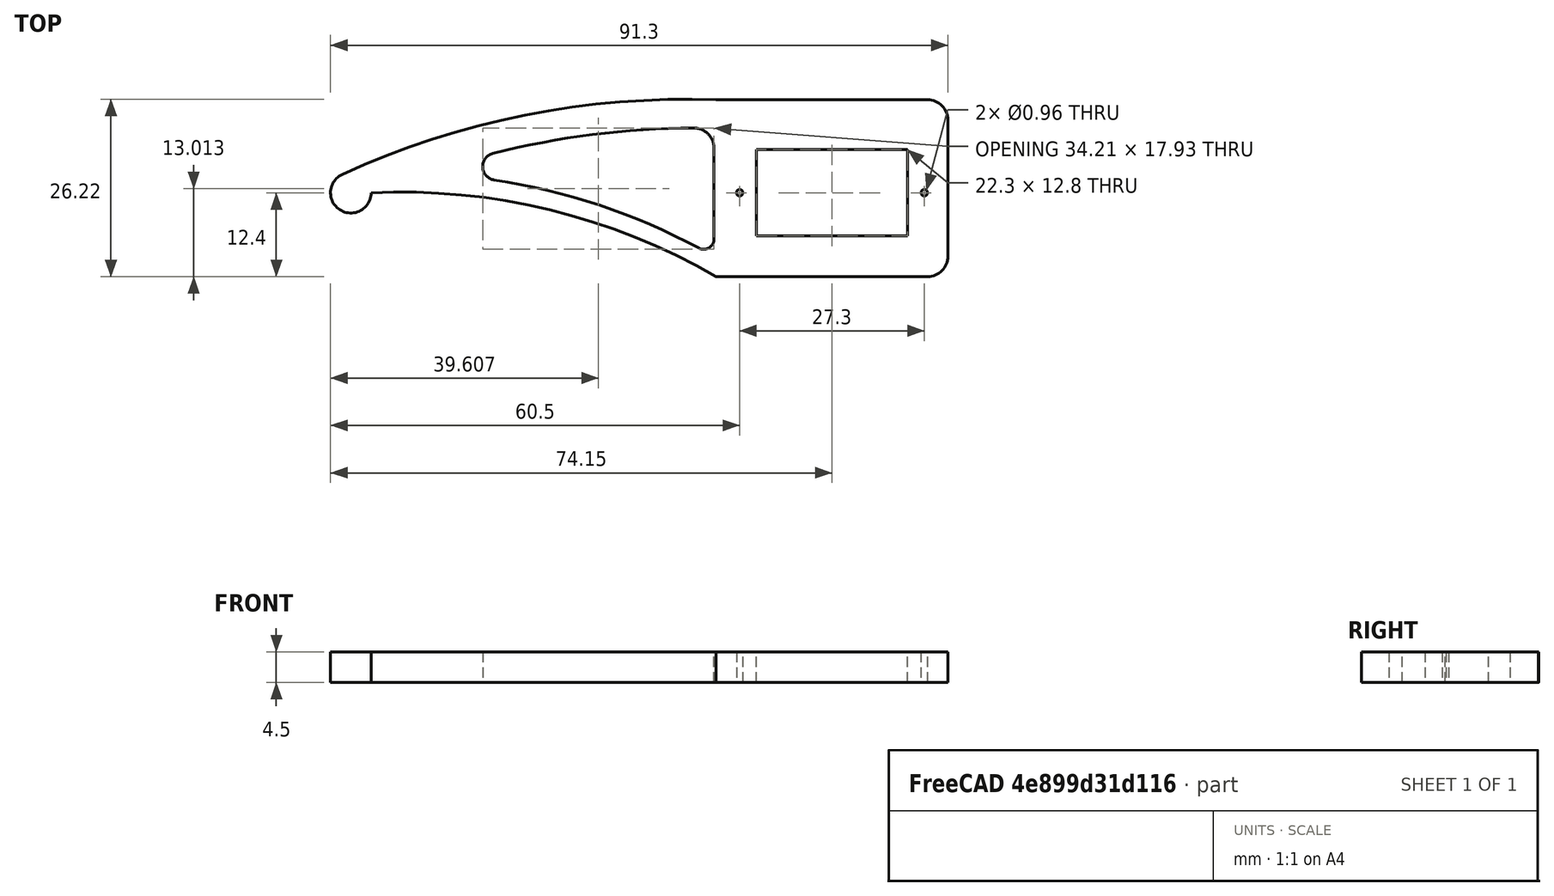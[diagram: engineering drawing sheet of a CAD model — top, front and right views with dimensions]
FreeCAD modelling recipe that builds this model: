
FCSTD DOCUMENT  (FreeCAD 0.21R33771 (Git))
Label: temp_work
License: All rights reserved
LicenseURL: https://en.wikipedia.org/wiki/All_rights_reserved
objects: Sketcher::SketchObject×1, PartDesign::Pad×1, PartDesign::Body×1
note: 4 computed .brp shape members not serialized (recipe doc carries the construction recipe); baked Part::Feature solids carry a one-line shape summary decoded from their .brp

FEATURE [Sketcher::SketchObject] Sketch
  FullyConstrained = true
  MapMode = 5
  Support = -> [XY_Plane]
  sketch-geometry (24):
    g0: LineSegment StartX=-11.15 StartY=-6.4 StartZ=0 EndX=-11.15 EndY=6.4 EndZ=0
    g1: LineSegment StartX=-11.15 StartY=6.4 StartZ=0 EndX=11.15 EndY=6.4 EndZ=0
    g2: LineSegment StartX=11.15 StartY=6.4 StartZ=0 EndX=11.15 EndY=-6.4 EndZ=0
    g3: LineSegment StartX=11.15 StartY=-6.4 StartZ=0 EndX=-11.15 EndY=-6.4 EndZ=0
    g4: GeomPoint X=0 Y=0 Z=0
    g5: LineSegment StartX=-17.44 StartY=6.58002 StartZ=0 EndX=-17.44 EndY=-6.81401 EndZ=0
    g6: LineSegment StartX=-17.15 StartY=-12.4 StartZ=0 EndX=14.15 EndY=-12.4 EndZ=0
    g7: LineSegment StartX=17.15 StartY=-9.4 StartZ=0 EndX=17.15 EndY=10.742 EndZ=0
    g8: LineSegment StartX=14.15 StartY=13.742 StartZ=0 EndX=-17.15 EndY=13.742 EndZ=0
    g9: GeomPoint X=0 Y=0 Z=0
    g10: ArcOfCircle CenterX=14.15 CenterY=10.742 CenterZ=0 NormalX=0 NormalY=0 NormalZ=1 AngleXU=0 Radius=3 StartAngle=0 EndAngle=1.5708
    g11: GeomPoint X=17.15 Y=13.742 Z=0
    g12: ArcOfCircle CenterX=14.15 CenterY=-9.4 CenterZ=0 NormalX=0 NormalY=0 NormalZ=1 AngleXU=0 Radius=3 StartAngle=4.71239 EndAngle=6.28319
    g13: GeomPoint X=17.15 Y=-12.4 Z=0
    g14: Circle CenterX=-13.65 CenterY=0 CenterZ=0 NormalX=0 NormalY=0 NormalZ=1 AngleXU=0 Radius=0.48
    g15: Circle CenterX=13.65 CenterY=0 CenterZ=0 NormalX=0 NormalY=0 NormalZ=1 AngleXU=0 Radius=0.48
    g16: ArcOfCircle CenterX=-71.15 CenterY=0 CenterZ=0 NormalX=0 NormalY=0 NormalZ=1 AngleXU=0 Radius=3 StartAngle=2.00057 EndAngle=6.28318
    g17: ArcOfCircle CenterX=-21.5667 CenterY=-108.178 CenterZ=0 NormalX=0 NormalY=0 NormalZ=1 AngleXU=0 Radius=122 StartAngle=1.53459 EndAngle=2.00057
    g18: ArcOfCircle CenterX=-20.0433 CenterY=-112.419 CenterZ=0 NormalX=0 NormalY=0 NormalZ=1 AngleXU=0 Radius=122 StartAngle=1.57413 EndAngle=1.82008
    g19: ArcOfCircle CenterX=-63.6795 CenterY=-92.6923 CenterZ=0 NormalX=0 NormalY=0 NormalZ=1 AngleXU=0 Radius=92.8 StartAngle=1.04559 EndAngle=1.61899
    g20: ArcOfCircle CenterX=-63.6996 CenterY=-89.8814 CenterZ=0 NormalX=0 NormalY=0 NormalZ=1 AngleXU=0 Radius=92.8 StartAngle=1.07694 EndAngle=1.42203
    g21: ArcOfCircle CenterX=-20.44 CenterY=6.58002 CenterZ=0 NormalX=0 NormalY=0 NormalZ=1 AngleXU=0 Radius=3 StartAngle=0 EndAngle=1.57413
    g22: ArcOfCircle CenterX=-18.98 CenterY=-6.81401 CenterZ=0 NormalX=0 NormalY=0 NormalZ=1 AngleXU=0 Radius=1.54 StartAngle=4.21853 EndAngle=6.28319
    g23: ArcOfCircle CenterX=-49.6483 CenterY=3.87146 CenterZ=0 NormalX=0 NormalY=0 NormalZ=1 AngleXU=0 Radius=2 StartAngle=1.82008 EndAngle=4.56362
  constraints (64):
    c: Coincident(g0,g1)
    c: Coincident(g1,g2)
    c: Coincident(g2,g3)
    c: Coincident(g3,g0)
    c: Horizontal(g1)
    c: Horizontal(g3)
    c: Vertical(g0)
    c: Vertical(g2)
    c: Symmetric(g1,g0,g4)
    c: Coincident(g4,g-1)
    c: DistanceX(g1,g1) = 22.3
    c: DistanceY(g0,g0) = 12.8
    c: Horizontal(g6)
    c: Horizontal(g8)
    c: Vertical(g5)
    c: Vertical(g7)
    c: Coincident(g9,g4)
    c: PointOnObject(g11,g7)
    c: PointOnObject(g11,g8)
    c: Tangent(g7,g10) = -1.5708
    c: Tangent(g8,g10) = -1.5708
    c: PointOnObject(g13,g6)
    c: PointOnObject(g13,g7)
    c: Tangent(g6,g12) = -1.5708
    c: Tangent(g7,g12) = -1.5708
    c: Radius(g10) = 3
    c: Radius(g12) = 3
    c: DistanceX(g1,g7) = 6
    c: DistanceY(g6,g2) = 6
    c: PointOnObject(g14,g-1)
    c: DistanceX(g14,g0) = 2.5
    c: Radius(g14) = 0.48
    c: PointOnObject(g15,g-1)
    c: DistanceX(g2,g15) = 2.5
    c: Radius(g15) = 0.48
    c: PointOnObject(g16,g-1)
    c: Radius(g16) = 3
    c: DistanceX(g16,g0) = 60
    c: Coincident(g17,g8)
    c: Radius(g17) = 122
    c: Radius(g18) = 122
    c: Coincident(g19,g6)
    c: Radius(g19) = 92.8
    c: Radius(g20) = 92.8
    c: Tangent(g16,g17) = -1.5708
    c: Coincident(g16,g19)
    c: Tangent(g18,g21) = -1.5708
    c: Tangent(g5,g21) = 1.5708
    c: Radius(g21) = 3
    c: Tangent(g5,g22) = 1.5708
    c: Tangent(g20,g22) = 1.5708
    c: Tangent(g18,g23) = -1.5708
    c: Tangent(g20,g23) = 1.5708
    c: Radius(g23) = 2
    c: Radius(g22) = 1.54
    c: DistanceY(g-1,g18) = 9.58
    c: DistanceX(g18,g-1) = 20.45
    c: DistanceX(g20,g-1) = 19.71
    c: DistanceY(g20,g-1) = 8.17
    c: DistanceX(g5,g-1) = 17.44
    c: DistanceX(g8,g-1) = 17.15
    c: DistanceX(g6,g-1) = 17.15
    c: DistanceX(g16,g5) = 50.71
    c: DistanceX(g16,g0) = 61.25
FEATURE [PartDesign::Pad] Pad
  Direction = (0,0,1)
  Length = 4.5
  Length2 = 10
  Profile = -> Sketch
  ReferenceAxis = -> Sketch [N_Axis]
  Type = 0
FEATURE [PartDesign::Body] Body
  Group = -> [Sketch,Pad]
  Origin = -> Origin
  Tip = -> Pad
